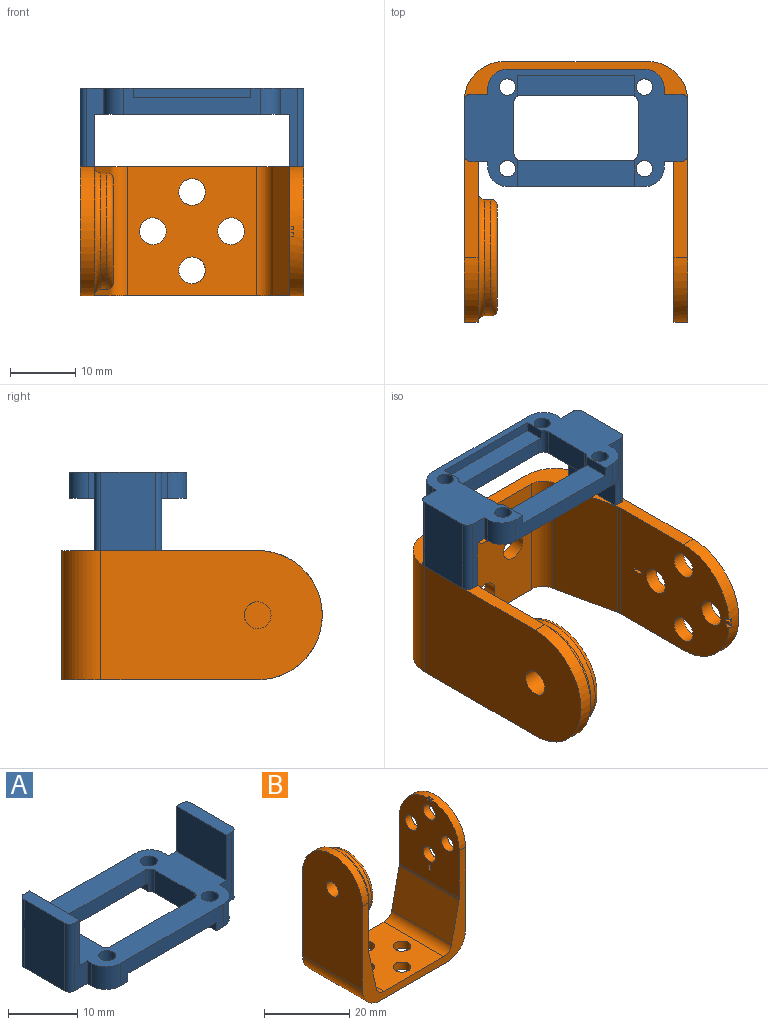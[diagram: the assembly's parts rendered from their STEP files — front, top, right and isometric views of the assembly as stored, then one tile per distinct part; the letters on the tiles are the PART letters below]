
ASSEMBLY  parts=2 mates=1
PART A: 45 faces, bbox 34.2x18x12 mm
  f0: plane 30x18mm, normal (0,0,1), area 300.4mm2, adj f1,f2,f3,f4,f5,f6,f7,f11
  f1: plane 21x4mm, normal (0,-1,0), area 57mm2, adj f0,f13,f14,f33,f38,f39,f40
  f2: plane 17x2.5mm, normal (0,-1,0), area 42.5mm2, adj f0,f5,f24,f35
  f3: plane 17x2.5mm, normal (0,1,0), area 42.5mm2, adj f0,f4,f26,f38
  f4: cylinder r=1mm len=4mm, axis (0,0,-1), area 5.5mm2, adj f0,f3,f27,f33,f38,f39
  f5: cylinder r=1mm len=4mm, axis (0,0,-1), area 5.5mm2, adj f0,f2,f27,f33,f35,f36
  f6: plane 4x0.85mm, normal (-1,0,0), area 3.4mm2, adj f0,f7,f32,f33
  f7: plane 12x2.6mm, normal (0,1,0), area 19.2mm2, adj f0,f6,f8,f33,f41,f42
  f8: cylinder r=1mm len=12mm, axis (0,0,-1), area 18.8mm2, adj f7,f9,f33,f42
  f9: plane 12x8.31mm, normal (-1,0,0), area 99.7mm2, adj f8,f10,f33,f42
  f10: cylinder r=1mm len=12mm, axis (0,0,-1), area 18.8mm2, adj f9,f11,f33,f42
  f11: plane 12x2.6mm, normal (0,-1,0), area 19.2mm2, adj f0,f10,f12,f33,f41,f42
  f12: plane 4x0.85mm, normal (-1,0,0), area 3.4mm2, adj f0,f11,f13,f33
  f13: cylinder r=3mm len=4mm, axis (0,0,-1), area 18.8mm2, adj f0,f1,f12,f33
  f14: cylinder r=3mm len=4mm, axis (0,0,-1), area 18.8mm2, adj f0,f1,f15,f33
  f15: plane 4x0.85mm, normal (1,0,0), area 3.4mm2, adj f0,f14,f16,f33
  f16: plane 12x2.6mm, normal (0,-1,0), area 19.2mm2, adj f0,f15,f17,f33,f43,f44
  f17: cylinder r=1mm len=12mm, axis (0,0,-1), area 18.8mm2, adj f16,f18,f33,f44
  f18: plane 12x8.31mm, normal (1,0,0), area 99.7mm2, adj f17,f19,f33,f44
  f19: cylinder r=1mm len=12mm, axis (0,0,-1), area 18.8mm2, adj f18,f20,f33,f44
  f20: plane 12x2.6mm, normal (0,1,0), area 19.2mm2, adj f0,f19,f21,f33,f43,f44
  f21: plane 4x0.85mm, normal (1,0,0), area 3.4mm2, adj f0,f20,f22,f33
  f22: cylinder r=3mm len=4mm, axis (0,0,-1), area 18.8mm2, adj f0,f21,f23,f33
  f23: plane 21x4mm, normal (0,1,0), area 84mm2, adj f0,f22,f32,f33
  f24: cylinder r=1mm len=4mm, axis (0,0,-1), area 5.5mm2, adj f0,f2,f25,f33,f35,f37
  f25: plane 8x4mm, normal (-1,0,0), area 32mm2, adj f0,f24,f26,f33
  f26: cylinder r=1mm len=4mm, axis (0,0,-1), area 5.5mm2, adj f0,f3,f25,f33,f38,f40
  f27: plane 8x4mm, normal (1,0,0), area 32mm2, adj f0,f4,f5,f33
  f28: cylinder r=1.25mm len=4mm, axis (0,0,-1), area 31.4mm2, adj f0,f33
  f29: cylinder r=1.25mm len=4mm, axis (0,0,-1), area 31.4mm2, adj f0,f33
  f30: cylinder r=1.25mm len=4mm, axis (0,0,-1), area 31.4mm2, adj f0,f33
  f31: cylinder r=1.25mm len=4mm, axis (0,0,-1), area 31.4mm2, adj f0,f33
  f32: cylinder r=3mm len=4mm, axis (0,0,-1), area 18.8mm2, adj f0,f6,f23,f33
  f33: plane 34.2x18mm, normal (0,0,-1), area 216.8mm2, adj f1,f4,f5,f6,f7,f8,f9,f10
  f34: plane 18x1.5mm, normal (0,-1,0), area 27mm2, adj f33,f35,f36,f37
  f35: plane 18x3.13mm, normal (0,0,-1), area 54mm2, adj f2,f5,f24,f34,f36,f37
  f36: plane 3.13x1.5mm, normal (1,0,0), area 4.7mm2, adj f5,f33,f34,f35
  f37: plane 3.13x1.5mm, normal (-1,0,0), area 4.7mm2, adj f24,f33,f34,f35
  f38: plane 18x4.13mm, normal (0,0,-1), area 72mm2, adj f1,f3,f4,f26,f39,f40
  f39: plane 4.13x1.5mm, normal (1,0,0), area 6.2mm2, adj f1,f4,f33,f38
  f40: plane 4.13x1.5mm, normal (-1,0,0), area 6.2mm2, adj f1,f26,f33,f38
  f41: plane 10.31x8mm, normal (1,0,0), area 82.5mm2, adj f0,f7,f11,f42
  f42: plane 10.31x2.1mm, normal (0,0,1), area 21.2mm2, adj f7,f8,f9,f10,f11,f41
  f43: plane 10.31x8mm, normal (-1,0,0), area 82.5mm2, adj f0,f16,f20,f44
  f44: plane 10.31x2.1mm, normal (0,0,1), area 21.2mm2, adj f16,f17,f18,f19,f20,f43
PART B: 44 faces, bbox 34.2x21.4x40.7 mm
  f0: plane 23.62x19.8mm, normal (-1,0,0), area 371.3mm2, adj f3,f8,f9,f10,f27,f28,f29,f30
  f1: cylinder r=2.6mm len=19.8mm, axis (0,-1,0), area 70mm2, adj f2,f4,f8,f9
  f2: plane 19.8x11.58mm, normal (-0.98,0,0.21), area 234.5mm2, adj f1,f3,f8,f9
  f3: cylinder r=2.6mm len=19.8mm, axis (0,-1,0), area 10.9mm2, adj f0,f2,f8,f9
  f4: plane 19.8x19.8mm, normal (0,0,1), area 339.2mm2, adj f1,f8,f9,f11,f12,f13,f16,f22
  f5: cylinder r=6mm len=19.8mm, axis (0,-1,0), area 186.6mm2, adj f6,f7,f8,f9
  f6: plane 33.9x19.8mm, normal (1,0,0), area 576.3mm2, adj f5,f8,f9,f10,f27,f28,f29,f30
  f7: plane 22.2x19.8mm, normal (0,0,-1), area 386.7mm2, adj f5,f8,f9,f11,f12,f13,f19,f22
  f8: plane 34.2x30mm, normal (0,1,0), area 217mm2, adj f0,f1,f2,f3,f4,f5,f6,f7
  f9: plane 34.2x30mm, normal (0,-1,0), area 217mm2, adj f0,f1,f2,f3,f4,f5,f6,f7
  f10: cylinder r=9.9mm len=19.8mm, axis (-1,0,0), area 64.8mm2, adj f0,f6,f8,f9,f31,f32,f33,f35
  f11: cylinder r=2.05mm len=4.1mm, axis (0,0,-1), area 27mm2, adj f4,f7
  f12: cylinder r=2.05mm len=4.1mm, axis (0,0,-1), area 27mm2, adj f4,f7
  f13: cylinder r=2.05mm len=4.1mm, axis (0,0,-1), area 27mm2, adj f4,f7
  f14: cylinder r=2.05mm len=5.05mm, axis (1,0,0), area 65mm2, adj f20,f23
  f15: plane 19.8x13.72mm, normal (1,0,0), area 117.8mm2, adj f8,f9,f18,f25
  f16: cylinder r=2.6mm len=19.8mm, axis (0,-1,0), area 70mm2, adj f4,f8,f9,f17
  f17: plane 19.8x11.58mm, normal (0.98,0,0.21), area 234.5mm2, adj f8,f9,f16,f18
  f18: cylinder r=2.6mm len=19.8mm, axis (0,-1,0), area 10.9mm2, adj f8,f9,f15,f17
  f19: cylinder r=6mm len=19.8mm, axis (0,-1,0), area 186.6mm2, adj f7,f8,f9,f20
  f20: plane 33.9x19.8mm, normal (-1,0,0), area 616mm2, adj f8,f9,f14,f19,f21
  f21: cylinder r=9.9mm len=19.8mm, axis (1,0,0), area 65.3mm2, adj f8,f9,f20,f25
  f22: cylinder r=2.05mm len=4.1mm, axis (0,0,-1), area 27mm2, adj f4,f7
  f23: plane 15.8x15.8mm, normal (1,0,0), area 182.9mm2, adj f14,f26
  f24: cylinder r=8.9mm len=17.8mm, axis (1,0,0), area 53.1mm2, adj f25,f26
  f25: torus R=9.9mm, axis (-1,0,0), area 91.4mm2, adj f15,f21,f24
  f26: torus R=7.9mm, axis (1,0,0), area 84.3mm2, adj f23,f24
  f27: cylinder r=2.05mm len=4.1mm, axis (-1,0,0), area 27mm2, adj f0,f6
  f28: cylinder r=2.05mm len=4.1mm, axis (-1,0,0), area 27mm2, adj f0,f6
  f29: cylinder r=2.05mm len=4.1mm, axis (-1,0,0), area 27mm2, adj f0,f6
  f30: cylinder r=2.05mm len=4.1mm, axis (-1,0,0), area 27mm2, adj f0,f6
  f31: plane 0.76x0.5mm, normal (0,1,0), area 0.4mm2, adj f0,f10,f33,f34
  f32: plane 0.73x0.5mm, normal (0,-1,0), area 0.4mm2, adj f0,f10,f33,f34
  f33: plane 0.76x0.5mm, normal (-1,0,0), area 0.4mm2, adj f10,f31,f32,f34
  f34: plane 0.5x0.5mm, normal (0,0,1), area 0.3mm2, adj f0,f31,f32,f33
  f35: plane 0.73x0.5mm, normal (0,1,0), area 0.4mm2, adj f0,f10,f37,f38
  f36: plane 0.76x0.5mm, normal (0,-1,0), area 0.4mm2, adj f0,f10,f37,f38
  f37: plane 0.76x0.5mm, normal (-1,0,0), area 0.4mm2, adj f10,f35,f36,f38
  f38: plane 0.5x0.5mm, normal (0,0,1), area 0.3mm2, adj f0,f35,f36,f37
  f39: plane 0.5x0.5mm, normal (0,0,1), area 0.3mm2, adj f0,f40,f42,f43
  f40: plane 1.5x0.5mm, normal (0,1,0), area 0.8mm2, adj f0,f39,f41,f43
  f41: plane 0.5x0.5mm, normal (0,0,-1), area 0.3mm2, adj f0,f40,f42,f43
  f42: plane 1.5x0.5mm, normal (0,-1,0), area 0.8mm2, adj f0,f39,f41,f43
  f43: plane 1.5x0.5mm, normal (-1,0,0), area 0.8mm2, adj f39,f40,f41,f42
PLACE A rot(axis=(0,1,0),180deg) t=(-9.79,-11.52,51.72)mm
PLACE B rot(axis=(1,0,0),90deg) t=(-9.79,-1.36,29.82)mm
MATE fastened B.f8 <-> A.f42  axis (0,0,1) through (7.31,-7.36,39.72)mm
